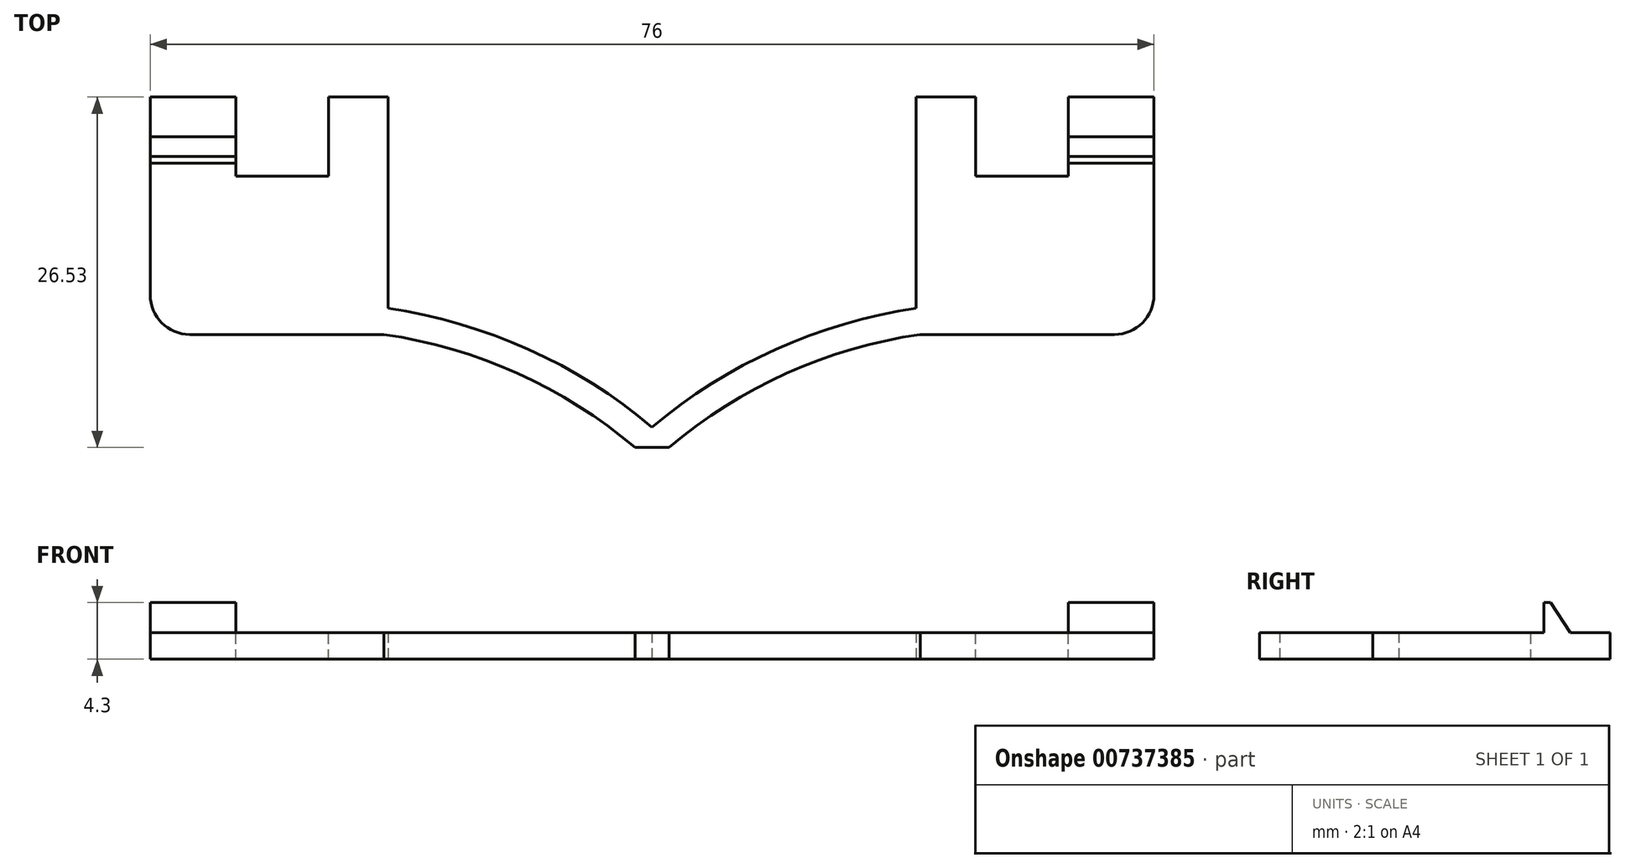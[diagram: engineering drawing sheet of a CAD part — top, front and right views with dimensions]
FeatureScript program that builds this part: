
annotation { "Feature Type Name" : "Feature", "Feature Type Description" : "" }
export const myFeature = defineFeature(function(context is Context, id is Id, definition is map)
    precondition{}
    {
        {
            var Q0;
            Q0=qCreatedBy(makeId("Top.planeOp"),FACE);
            var sketch = newSketch(context, id + "F0", { "sketchPlane" : qUnion([Q0])});
            skLineSegment(sketch, "E0", {"start": v(0, 63.43) * mm, "end": v(0, -55.17) * mm, "construction": true});
            skLineSegment(sketch, "E1.0", {"start": v(-40, 63.43) * mm, "end": v(-40, -55.17) * mm, "construction": true});
            skLineSegment(sketch, "E2", {"start": v(-100.87, 0) * mm, "end": v(136.87, 0) * mm, "construction": true});
            skLineSegment(sketch, "E3", {"start": v(-40, 0) * mm, "end": v(-58, 0) * mm});
            skLineSegment(sketch, "E4", {"start": v(0, 0) * mm, "end": v(18, 0) * mm});
            skLineSegment(sketch, "E5", {"start": v(-40, 0) * mm, "end": v(-40, -16) * mm});
            skLineSegment(sketch, "E6", {"start": v(0, 0) * mm, "end": v(0, -16) * mm});
            skLineSegment(sketch, "E7", {"start": v(-40, 57.65) * mm, "end": v(0, 57.65) * mm, "construction": true});
            skLineSegment(sketch, "E8", {"start": v(-20, 0) * mm, "end": v(-20, -25) * mm, "construction": true});
            skPoint(sketch, "E8.startSnap0", {"position": v(-20, 57.65) * mm});
            skArc(sketch, "E9", {"start": v(0, -16) * mm, "mid": v(-10.63, -19.1) * mm, "end": v(-20, -25) * mm});
            skArc(sketch, "E10", {"start": v(-20, -25) * mm, "mid": v(-29.37, -19.1) * mm, "end": v(-40, -16) * mm});
            skArc(sketch, "E11.0", {"start": v(0.29, -17.98) * mm, "mid": v(-9.8, -20.93) * mm, "end": v(-18.71, -26.53) * mm});
            skArc(sketch, "E12.0", {"start": v(-21.29, -26.53) * mm, "mid": v(-30.2, -20.93) * mm, "end": v(-40.29, -17.98) * mm});
            skLineSegment(sketch, "E13", {"start": v(-21.29, -26.53) * mm, "end": v(-18.71, -26.53) * mm});
            skLineSegment(sketch, "E14", {"start": v(-58, 0) * mm, "end": v(-58, -14.98) * mm});
            skLineSegment(sketch, "E15", {"start": v(-55, -17.98) * mm, "end": v(-40.29, -17.98) * mm});
            skLineSegment(sketch, "E16", {"start": v(18, 0) * mm, "end": v(18, -14.98) * mm});
            skLineSegment(sketch, "E17", {"start": v(15, -17.98) * mm, "end": v(0.29, -17.98) * mm});
            skPoint(sketch, "E18.visualSharp", {"position": v(-58, -17.98) * mm});
            skArc(sketch, "E18.filletArc", {"start": v(-58, -14.98) * mm, "mid": v(-57.12, -17.1) * mm, "end": v(-55, -17.98) * mm});
            skPoint(sketch, "E19.visualSharp", {"position": v(18, -17.98) * mm});
            skArc(sketch, "E19.filletArc", {"start": v(15, -17.98) * mm, "mid": v(17.12, -17.1) * mm, "end": v(18, -14.98) * mm});
            skSolve(sketch);
        }
        {
            var Q0;
            Q0 = qSketchRegion(id + "F0", true);
            extrude(context, id + "F1", {"entities" : qUnion([Q0]), "depth" : 2 * mm, "offsetDistance" : 25 * mm});
        }
        {
            var Q0;
            Q0=makeQuery(id+"F1.opExtrude","CAP_FACE",FACE,{"disambiguationData":[OSD([sQuery(id+"F0.wireOp",EDGE,"E3"),sQuery(id+"F0.wireOp",EDGE,"E4"),sQuery(id+"F0.wireOp",EDGE,"E5"),sQuery(id+"F0.wireOp",EDGE,"E6"),sQuery(id+"F0.wireOp",EDGE,"E9"),sQuery(id+"F0.wireOp",EDGE,"E10"),sQuery(id+"F0.wireOp",EDGE,"E11.0"),sQuery(id+"F0.wireOp",EDGE,"E12.0"),sQuery(id+"F0.wireOp",EDGE,"E13"),sQuery(id+"F0.wireOp",EDGE,"E14"),sQuery(id+"F0.wireOp",EDGE,"E15"),sQuery(id+"F0.wireOp",EDGE,"E16"),sQuery(id+"F0.wireOp",EDGE,"E17"),sQuery(id+"F0.wireOp",EDGE,"E18.filletArc"),sQuery(id+"F0.wireOp",EDGE,"E19.filletArc")])],"isStart":false});
            var sketch = newSketch(context, id + "F2", { "sketchPlane" : qUnion([Q0])});
            skLineSegment(sketch, "E20", {"start": v(-20, 18.5) * mm, "end": v(-20, -55.28) * mm, "construction": true});
            skLineSegment(sketch, "E21.0", {"start": v(-44.5, 18.5) * mm, "end": v(-44.5, -55.28) * mm, "construction": true});
            skLineSegment(sketch, "E22", {"start": v(-82.47, 0) * mm, "end": v(39.66, 0) * mm, "construction": true});
            skLineSegment(sketch, "E23.0", {"start": v(-82.47, -6) * mm, "end": v(39.66, -6) * mm, "construction": true});
            skLineSegment(sketch, "E24.0", {"start": v(-51.5, 18.5) * mm, "end": v(-51.5, -55.28) * mm, "construction": true});
            skLineSegment(sketch, "E25.bottom", {"start": v(-51.5, 0) * mm, "end": v(-44.5, 0) * mm});
            skLineSegment(sketch, "E25.top", {"start": v(-51.5, -6) * mm, "end": v(-44.5, -6) * mm});
            skLineSegment(sketch, "E25.left", {"start": v(-51.5, 0) * mm, "end": v(-51.5, -6) * mm});
            skLineSegment(sketch, "E25.right", {"start": v(-44.5, 0) * mm, "end": v(-44.5, -6) * mm});
            skLineSegment(sketch, "E26.MirrorCS", {"start": v(11.5, 0) * mm, "end": v(11.5, -6) * mm});
            skLineSegment(sketch, "E27.MirrorCS", {"start": v(11.5, -6) * mm, "end": v(4.5, -6) * mm});
            skLineSegment(sketch, "E28.MirrorCS", {"start": v(4.5, 0) * mm, "end": v(4.5, -6) * mm});
            skLineSegment(sketch, "E29.MirrorCS", {"start": v(11.5, 0) * mm, "end": v(4.5, 0) * mm});
            skSolve(sketch);
        }
        {
            var Q0;
            Q0 = qSketchRegion(id + "F2", true);
            extrude(context, id + "F3", {"entities" : qUnion([Q0]), "operationType" : NewBodyOperationType.REMOVE, "endBound" : BoundingType.UP_TO_NEXT, "oppositeDirection" : true, "depth" : 25 * mm, "offsetDistance" : 25 * mm});
        }
        {
            var Q0;
            Q0=makeQuery(id+"F1.opExtrude","SWEPT_FACE",FACE,{"disambiguationData":[OSD([sQuery(id+"F0.wireOp",EDGE,"E14")])]});
            var sketch = newSketch(context, id + "F4", { "sketchPlane" : qUnion([Q0])});
            skLineSegment(sketch, "E30", {"start": v(0, 18.14) * mm, "end": v(0, -13.77) * mm, "construction": true});
            skLineSegment(sketch, "E31.0", {"start": v(3, 18.14) * mm, "end": v(3, -13.77) * mm, "construction": true});
            skLineSegment(sketch, "E32", {"start": v(3, 2) * mm, "end": v(5, 2) * mm});
            skLineSegment(sketch, "E33", {"start": v(5, 2) * mm, "end": v(5, 4.3) * mm});
            skLineSegment(sketch, "E34", {"start": v(5, 4.3) * mm, "end": v(4.5, 4.3) * mm});
            skLineSegment(sketch, "E35", {"start": v(4.5, 4.3) * mm, "end": v(3, 2) * mm});
            skSolve(sketch);
        }
        {
            var Q0;
            Q0 = qSketchRegion(id + "F4", true);
            var Q1;
            Q1=makeQuery(id+"F3.boolean.opBoolean","COPY",FACE,{"derivedFrom":makeQuery(id+"F3.opExtrude","SWEPT_FACE",FACE,{"disambiguationData":[OSD([sQuery(id+"F2.wireOp",EDGE,"E25.left")])]})});
            extrude(context, id + "F5", {"entities" : qUnion([Q0]), "operationType" : NewBodyOperationType.ADD, "endBound" : BoundingType.UP_TO_SURFACE, "oppositeDirection" : true, "depth" : 25 * mm, "endBoundEntityFace" : qUnion([Q1]), "offsetDistance" : 25 * mm});
        }
        {
            var Q0;
            Q0=makeQuery(id+"F1.opExtrude","SWEPT_FACE",FACE,{"disambiguationData":[OSD([sQuery(id+"F0.wireOp",EDGE,"E16")])]});
            var sketch = newSketch(context, id + "F6", { "sketchPlane" : qUnion([Q0])});
            skLineSegment(sketch, "E36.0", {"start": v(-4.5, 4.3) * mm, "end": v(-5, 4.3) * mm});
            skLineSegment(sketch, "E37.0", {"start": v(-3, 2) * mm, "end": v(-4.5, 4.3) * mm});
            skLineSegment(sketch, "E38.0", {"start": v(-5, 4.3) * mm, "end": v(-5, 2) * mm});
            skLineSegment(sketch, "E39", {"start": v(-5, 2) * mm, "end": v(-3, 2) * mm});
            skSolve(sketch);
        }
        {
            var Q0;
            Q0 = qSketchRegion(id + "F6", true);
            var Q1;
            Q1=makeQuery(id+"F3.boolean.opBoolean","COPY",FACE,{"derivedFrom":makeQuery(id+"F3.opExtrude","SWEPT_FACE",FACE,{"disambiguationData":[OSD([sQuery(id+"F2.wireOp",EDGE,"E26.MirrorCS")])]})});
            extrude(context, id + "F7", {"entities" : qUnion([Q0]), "operationType" : NewBodyOperationType.ADD, "endBound" : BoundingType.UP_TO_SURFACE, "oppositeDirection" : true, "depth" : 25 * mm, "endBoundEntityFace" : qUnion([Q1]), "offsetDistance" : 25 * mm});
        }
    });
